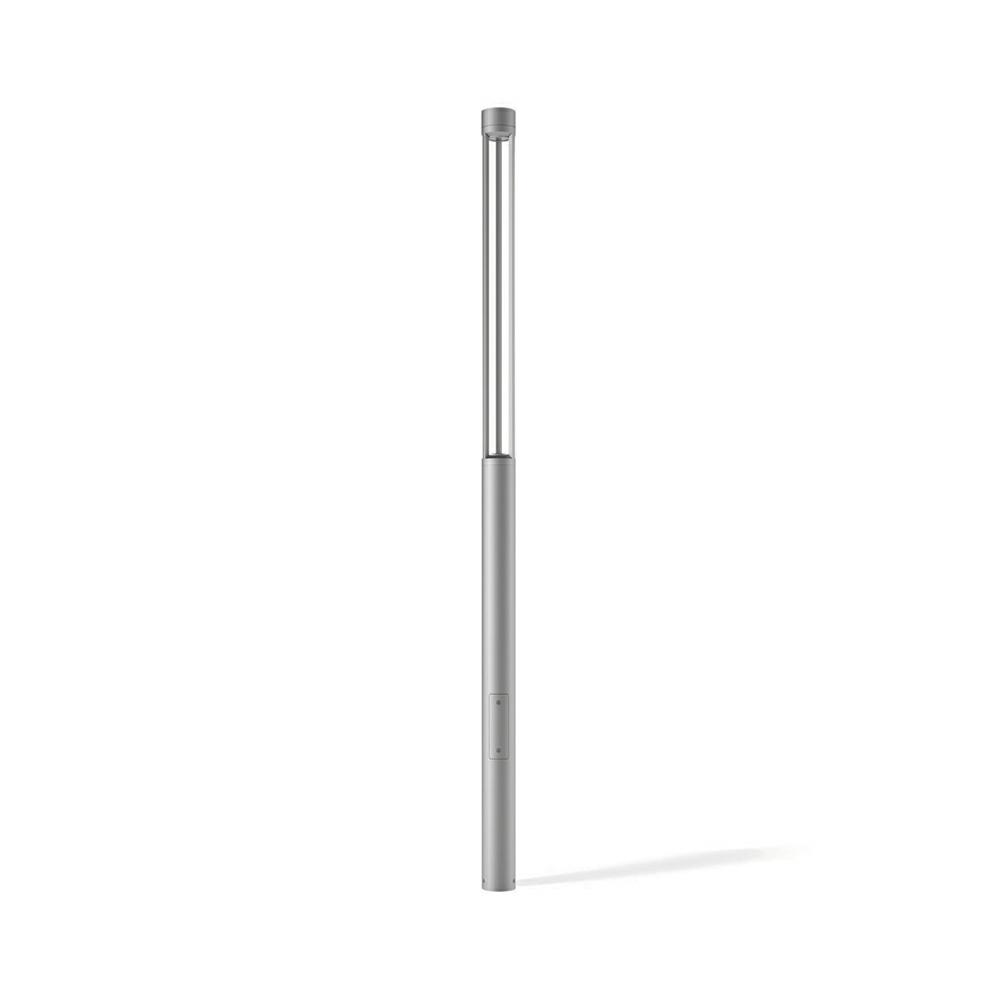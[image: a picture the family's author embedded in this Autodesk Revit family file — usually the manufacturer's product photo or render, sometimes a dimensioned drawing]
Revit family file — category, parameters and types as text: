
# Revit family: Platek_Tris
name_source: partatom
category: Apparecchi per illuminazione
revit_build: Autodesk Revit 2017 (Build: 20160225_1515(x64)
units: mm (PartAtom-declared; Revit-internal decimal feet)

## family parameters
Basato su piano di lavoro = No
Condiviso = No
Punto di calcolo locali = No
Quota connettore circolare = Usa diametro
Sempre verticale = Sì
Sorgente d'illuminazione = Sì
Taglio con vuoti quando caricato = No
Tipo di parte = Normale

## types (4) — shared parameters
Angolo inclinazione = 90.00°
Beam Angle = 0.00°
Body = PLK_Grey
CRI = >80
Carico apparente = 0 VA
Colour Temperature = 3000 K
Commenti sul tipo = Pedestrian areas, Urban zones, Paths, Roads
Descrizione = Outdoor Lighting, Floor/Ground Illumination
Diffuse Type = PMMA
Dimmable = No
Emetti da diametro cerchio = 45 mm  [stored 0.147638 ft]
Energy Efficiency Rating = A/A+/A++
Filtro dei colori = 16777215
Frequency = 50/60 Hz
Insulation Class = 2
LED Protection = Surge protection included
Lampada = LED
Light Source = PLK_Light Source
Manufacturer Comment = 4mm anti-glare clear
Modello = Tris
Mounting Type = Ground
Nota chiave = Other Led colors available on request
PLATEK FInishes = Painted Aluminium Avalaible in Anthracite/Black/White/Corten/Bronze
Power Supply Unit = Included
Product Documentation Link = http://www.platek.eu
Product Page URL = http://www.platek.eu
Produttore = PLATEK SRL
Rendi la forma visibile nel rendering = No
Supply Voltage = 230 V
Supply Voltage Max = 240 V
Supply Voltage Min = 220 V
URL = www.platek.eu
Variazione temperatura colore lampada con luminosità attenuata = <Nessuno>

## per-type parameters (varying)
| type | Aluminium | Cable Lenght | Codice assieme | File diagramma fotometrico | H Body1800 | H Body2600 | H Body3600 | H Body900 | H Light1800 | H Light2600 | H Light3600 | H Light900 | Height Body | Height Light | IK Rating | IP Rating | Immagine tipo | Luminaire Luminous Flux | Luminaire Luminous Intensity | Luminaire Wattage | PLATEK Article Code | Product Dimension |
| 3333611_20,8W_LED_3000K_H900mm | PLK_Light Source |  | 3333611.06(Grey); 3333611.08(Anthracite); 3333611.01(Black); 3333611.02(White); 3333611.07(Corten); 3333611.09(Bronze) | 3333611.ies | No | No | No | Sì | No | No | No | Sì | 229 mm | 520 mm  [stored 1.70604 ft] | IK 10 | IP66 | tris_900.jpg | 2067 lm | 927 cd | 21 W | 3333611 | Ø160mm x H900mm |
| 3333612_29,5W_LED_3000K_H1800mm | PLK_Light Source | Ø 4÷6mm | 3333612.06(Grey); 3333612.08(Anthracite); 3333612.01(Black); 3333612.02(White); 3333612.07(Corten); 3333612.09(Bronze) | 3333612.IES | Sì | No | No | No | Sì | No | No | No | 856 mm  [stored 2.8084 ft] | 793 mm  [stored 2.60171 ft] | IK 10 | IP66 | tris_1800.jpg | 3011 lm | 1351 cd | 30 W | 3333612 | Ø160mm x H1800mm |
| 3333613_45W_LED_3000K_H3600mm | PLK_Aluminium |  | 3333613.06(Grey); 3333613.08(Anthracite); 3333613.01(Black); 3333613.02(White); 3333613.07(Corten); 3333613.09(Bronze) | 3333613.IES | No | No | Sì | No | No | No | Sì | No | 1949 mm  [stored 6.39436 ft] | 1500 mm  [stored 4.92126 ft] | IK 07 | IP65 | tris_3600.jpg | 4517 lm | 2027 cd | 45 W | 3333613 | Ø160mm x H3600mm |
| 3333614_45W_LED_3000K_H2600mm | PLK_Light Source |  | 3333614.06(Grey); 3333614.08(Anthracite); 3333614.01(Black); 3333614.02(White); 3333614.07(Corten); 3333614.09(Bronze) | 3333614.IES | No | Sì | No | No | No | Sì | No | No | 949 mm  [stored 3.11352 ft] | 1500 mm  [stored 4.92126 ft] | IK 10 | IP66 | tris_2600.jpg | 4517 lm | 2027 cd | 45 W | 3333614 | Ø160mm x H2600mm |

note: [stored X ft] marks values corroborated as IEEE doubles in the binary element streams (Revit-internal decimal feet)
